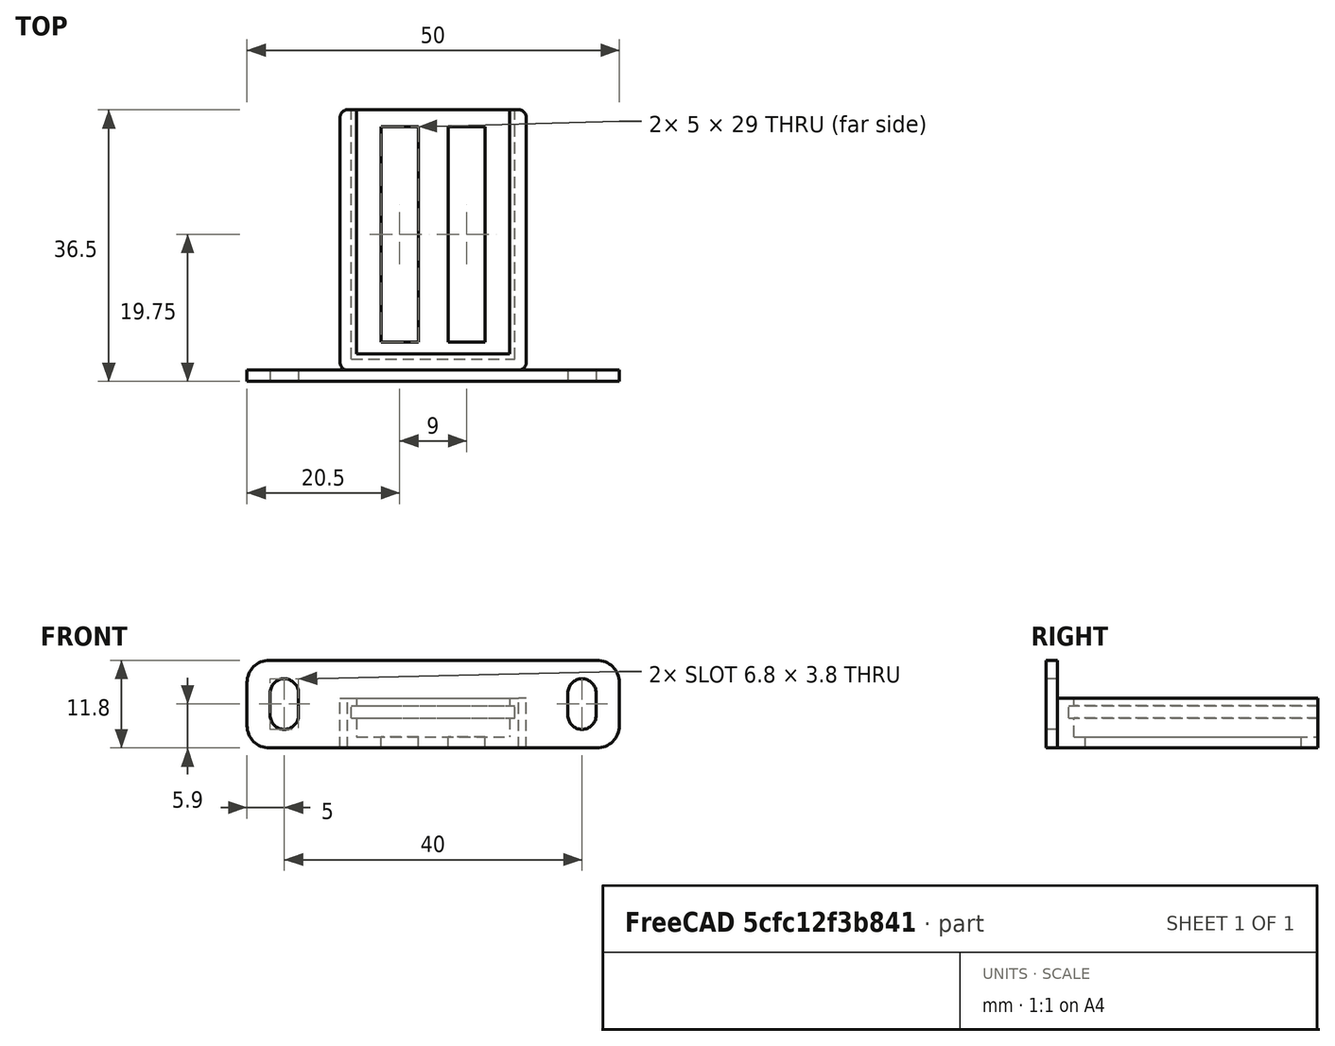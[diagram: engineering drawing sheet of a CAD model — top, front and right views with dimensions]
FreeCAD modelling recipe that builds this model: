
FCSTD DOCUMENT  (FreeCAD 0.19R23578 (Git))
Label: lj245a_voltage_translator
License: FreeArt
LicenseURL: http://artlibre.org/licence/lal
objects: Part::Box×5, Part::MultiFuse×3, Spreadsheet::Sheet×2, Part::Fillet×1, Part::Feature×1, Part::Cut×1, App::Part×1
note: 11 computed .brp shape members not serialized (recipe doc carries the construction recipe); baked Part::Feature solids carry a one-line shape summary decoded from their .brp

FEATURE [Spreadsheet::Sheet] Spreadsheet  label="p"
  cells = A1=pcb_x; B1(pcb_x)=22; A2=pcb_y; B2(pcb_y)=33.5; A3=pcb_z; B3(pcb_z)=1.7; A4=pcb_under; B4(pcb_under)=2.5; A5=side_wall; B5(side_wall)=1.5; A6=pcb_side_lane; B6(pcb_side_lane)=0.7; A7=bottom_wall; B7(bottom_wall)=1.5; A8=pcb_above; B8(pcb_above)=1
FEATURE [Part::Box] Box  label="external cube"
  AttacherType = Attacher::AttachEngine3D
  Height = 6.7
  Length = 25
  Width = 35
  expr: Length = <<p>>.pcb_x + 2 * <<p>>.side_wall
  expr: Width = <<p>>.pcb_y + <<p>>.side_wall
  expr: Height = <<p>>.bottom_wall + <<p>>.pcb_under + <<p>>.pcb_z + <<p>>.pcb_above
FEATURE [Part::Box] Box006  label="internal cube"
  AttacherType = Attacher::AttachEngine3D
  Height = 5.2
  Length = 20.6
  Placement = pos=(2.2,2.2,1.5) rot=(0,0,1;0rad)
  Width = 33.6
  expr: Length = <<p>>.pcb_x - 2 * <<p>>.pcb_side_lane
  expr: Width = <<p>>.pcb_y - 2 * <<p>>.pcb_side_lane + <<p>>.side_wall
  expr: Height = <<p>>.pcb_under + <<p>>.pcb_z + <<p>>.pcb_above
  expr: .Placement.Base.z = <<p>>.bottom_wall
  expr: .Placement.Base.x = <<p>>.side_wall + <<p>>.pcb_side_lane
  expr: .Placement.Base.y = <<p>>.side_wall + <<p>>.pcb_side_lane
FEATURE [Part::Box] Box007  label="pcb extract cube"
  AttacherType = Attacher::AttachEngine3D
  Height = 1.7
  Length = 22
  Placement = pos=(1.5,1.5,4) rot=(0,0,1;0rad)
  Width = 33.5
  expr: Height = <<p>>.pcb_z
  expr: .Placement.Base.z = <<p>>.bottom_wall + <<p>>.pcb_under
  expr: Width = <<p>>.pcb_y
  expr: Length = <<p>>.pcb_x
  expr: .Placement.Base.x = <<p>>.side_wall
  expr: .Placement.Base.y = <<p>>.side_wall
FEATURE [Part::Fillet] Fillet  label="external fillet"
  Base = -> Box
  Edges = 4 edges r=1: [Edge1,Edge3,Edge5,Edge7]
FEATURE [Part::Feature] Body002  label="attach plane x rotated dir001"
  Placement = pos=(-12.5,0,0) rot=(1,0,0;1.5708rad)
  shape: bbox 50 x 1.5 x 11.8 mm, 18 faces (baked)
FEATURE [Part::MultiFuse] Fusion001  label="body fusion"
  Shapes = -> [Fillet,Body002]
FEATURE [Spreadsheet::Sheet] Spreadsheet001  label="vhp"
  cells = A1=view_hole_x; B1(view_hole_x)=5; A2=view_hole_y; B2(view_hole_y)=29; A3=hole_narrow_offset_x; B3(hole_narrow_offset_x)=4; A4=hole_wide_offset_x; B4(hole_wide_offset_x)=4
FEATURE [Part::Box] Box009  label="central view hole001"
  AttacherType = Attacher::AttachEngine3D
  Height = 10
  Length = 5
  Placement = pos=(14.5,0,0) rot=(0,0,1;0rad)
  Width = 29
  expr: Width = <<vhp>>.view_hole_y
  expr: Length = <<vhp>>.view_hole_x
  expr: .Placement.Base.x = <<p>>.side_wall + <<p>>.pcb_x - <<vhp>>.hole_narrow_offset_x - <<vhp>>.view_hole_x
FEATURE [Part::Box] Box008  label="central view hole"
  AttacherType = Attacher::AttachEngine3D
  Height = 10
  Length = 5
  Placement = pos=(5.5,0,0) rot=(0,0,1;0rad)
  Width = 29
  expr: Length = <<vhp>>.view_hole_x
  expr: Width = <<vhp>>.view_hole_y
  expr: .Placement.Base.x = <<p>>.side_wall + <<vhp>>.hole_wide_offset_x
FEATURE [Part::MultiFuse] Fusion002  label="view hole fusion"
  Placement = pos=(0,3.75,0) rot=(0,0,1;0rad)
  Shapes = -> [Box008,Box009]
  expr: .Placement.Base.y = <<p>>.side_wall + (<<p>>.pcb_y - <<vhp>>.view_hole_y) / 2
FEATURE [Part::MultiFuse] Fusion  label="extract fusion"
  Shapes = -> [Box006,Box007,Fusion002]
FEATURE [Part::Cut] Cut  label="body cut"
  Base = -> Fusion001
  Tool = -> Fusion
FEATURE [App::Part] Part  label="pcb box part"
  Group = -> [Box,Fillet,Fusion001,Fusion,Box007,Box006,Cut]
  Origin = -> Origin
